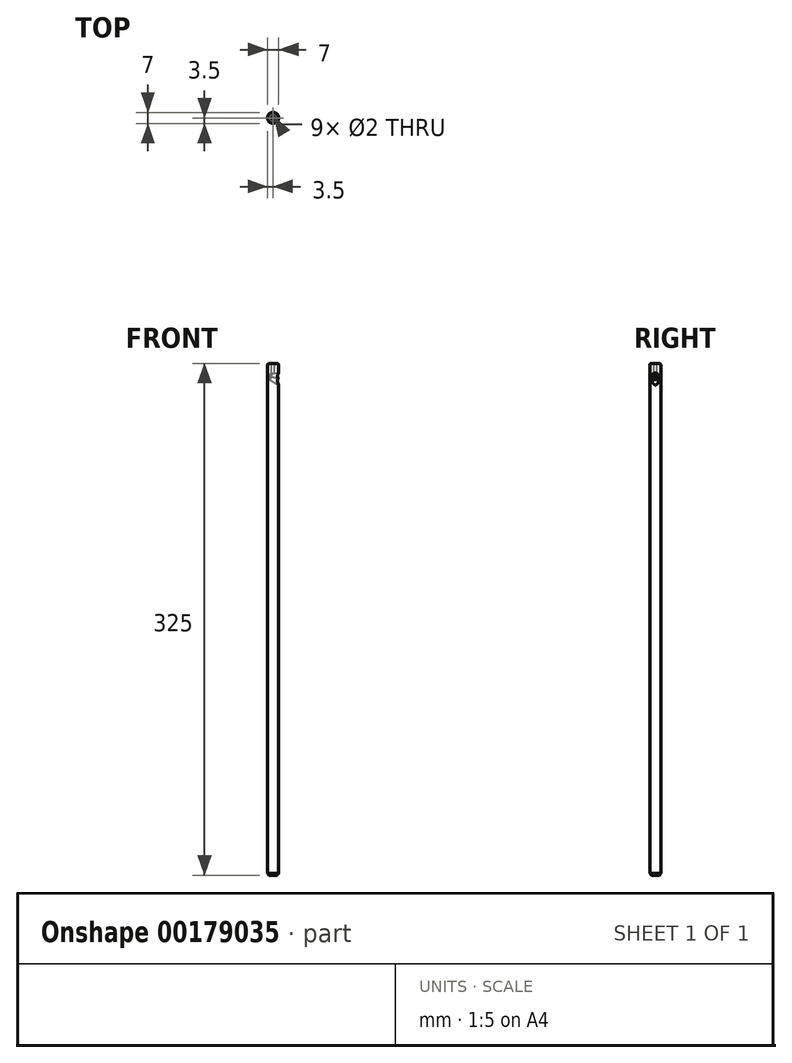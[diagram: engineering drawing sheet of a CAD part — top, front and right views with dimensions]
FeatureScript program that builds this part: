
annotation { "Feature Type Name" : "Feature", "Feature Type Description" : "" }
export const myFeature = defineFeature(function(context is Context, id is Id, definition is map)
    precondition{}
    {
        {
            var Q0;
            Q0=qCreatedBy(makeId("Front.planeOp"),FACE);
            var sketch = newSketch(context, id + "F0", { "sketchPlane" : qUnion([Q0])});
            skLineSegment(sketch, "E0", {"start": v(-3.5, 1) * mm, "end": v(-3.5, 324) * mm});
            skLineSegment(sketch, "E1", {"start": v(-1, 323.5) * mm, "end": v(-1, 318) * mm});
            skLineSegment(sketch, "E2", {"start": v(-1, 318) * mm, "end": v(0, 317.42) * mm});
            skArc(sketch, "E3", {"start": v(-1, 323.5) * mm, "mid": v(-1.44, 324.56) * mm, "end": v(-2.5, 325) * mm});
            skArc(sketch, "E4", {"start": v(-2.5, 325) * mm, "mid": v(-3.2, 324.7) * mm, "end": v(-3.5, 324) * mm});
            skLineSegment(sketch, "E5", {"start": v(-3.5, 1) * mm, "end": v(-2.5, 0) * mm});
            skLineSegment(sketch, "E6", {"start": v(-2.5, 0) * mm, "end": v(0, 0) * mm});
            skPoint(sketch, "E7.orphan", {"position": v(-3.5, 0) * mm});
            skPoint(sketch, "E8.MirrorCS.start.orphan", {"position": v(3.5, 0) * mm});
            skLineSegment(sketch, "E9", {"start": v(0, 317.42) * mm, "end": v(0, 0) * mm});
            skLineSegment(sketch, "E10.MirrorCS", {"start": v(1, 323.5) * mm, "end": v(1, 318) * mm, "construction": true});
            skLineSegment(sketch, "E11", {"start": v(-2.5, 325) * mm, "end": v(1, 325) * mm, "construction": true});
            skSolve(sketch);
        }
        {
            var Q0;
            Q0 = qSketchRegion(id + "F0", true);
            var Q1;
            Q1=sQuery(id+"F0.wireOp",EDGE,"E9");
            revolve(context, id + "F1", {"entities" : qUnion([Q0]), "axis" : qUnion([Q1]), "revolveType" : RevolveType.FULL});
        }
        {
            var Q0;
            Q0=qCreatedBy(makeId("Front.planeOp"),FACE);
            var sketch = newSketch(context, id + "F2", { "sketchPlane" : qUnion([Q0])});
            skLineSegment(sketch, "E12", {"start": v(-2.15, 317) * mm, "end": v(-1, 319) * mm});
            skLineSegment(sketch, "E13", {"start": v(-1, 319) * mm, "end": v(10.58, 319) * mm});
            skLineSegment(sketch, "E14", {"start": v(-2.15, 317) * mm, "end": v(17.02, 317) * mm});
            skLineSegment(sketch, "E15.MirrorCS", {"start": v(-1, 315) * mm, "end": v(10.58, 315) * mm, "construction": true});
            skLineSegment(sketch, "E16.MirrorCS", {"start": v(-2.15, 317) * mm, "end": v(-1, 315) * mm, "construction": true});
            skLineSegment(sketch, "E17", {"start": v(-3.5, 1) * mm, "end": v(-3.5, 324.25) * mm, "construction": true});
            skLineSegment(sketch, "E18", {"start": v(10.58, 319) * mm, "end": v(10.58, 317) * mm});
            skLineSegment(sketch, "E19", {"start": v(1, 323.5) * mm, "end": v(1, 319) * mm, "construction": true});
            skLineSegment(sketch, "E20", {"start": v(-1, 319) * mm, "end": v(-1, 323.5) * mm, "construction": true});
            skLineSegment(sketch, "E21.0", {"start": v(-2.5, 325) * mm, "end": v(2.5, 325) * mm});
            skSolve(sketch);
        }
        {
            var Q0;
            Q0 = qSketchRegion(id + "F2", true);
            var Q1;
            Q1=sQuery(id+"F2.wireOp",EDGE,"E14");
            revolve(context, id + "F3", {"operationType" : NewBodyOperationType.REMOVE, "entities" : qUnion([Q0]), "axis" : qUnion([Q1]), "revolveType" : RevolveType.FULL, "oppositeDirection" : true});
        }
        {
            var Q0;
            Q0=qCreatedBy(makeId("Front.planeOp"),FACE);
            var sketch = newSketch(context, id + "F4", { "sketchPlane" : qUnion([Q0])});
            skLineSegment(sketch, "E22", {"start": v(3.5, 315) * mm, "end": v(-1.25, 315) * mm});
            skLineSegment(sketch, "E23.0", {"start": v(-1, 319) * mm, "end": v(-1, 315) * mm});
            skLineSegment(sketch, "E24", {"start": v(-1.06, 315.1) * mm, "end": v(-2.15, 317) * mm});
            skLineSegment(sketch, "E25", {"start": v(-2.15, 317) * mm, "end": v(-1.06, 318.9) * mm});
            skLineSegment(sketch, "E26", {"start": v(-2.15, 317) * mm, "end": v(-2.15, 314.7) * mm});
            skLineSegment(sketch, "E27", {"start": v(-2.15, 314.7) * mm, "end": v(6.5, 309.7) * mm});
            skLineSegment(sketch, "E28", {"start": v(-2.15, 317) * mm, "end": v(7.5, 311.42) * mm});
            skLineSegment(sketch, "E29", {"start": v(6.5, 309.7) * mm, "end": v(7.5, 311.42) * mm});
            skSolve(sketch);
        }
        {
            var Q0;
            {var subQ7=sQuery(id+"F4.wireOp",EDGE,"E26");Q0=makeQuery(id+"F4.imprint","IMPRINT",FACE,{"disambiguationData":[TD([[makeQuery(id+"F4.imprint","IMPRINT",EDGE,{"derivedFrom":subQ7}),1.0]])]});}
            var Q1;
            {var subQ0=sQuery(id+"F4.wireOp",EDGE,"E23.0");var subQ1=sQuery(id+"F4.wireOp",EDGE,"E22");var subQ2=makeQuery(id+"F4.imprint","INTERSECT",VERTEX,{"derivedFrom":[subQ1,subQ0]});Q1=makeQuery(id+"F4.imprint","IMPRINT",FACE,{"disambiguationData":[TD([[makeQuery(id+"F4.imprint","IMPRINT",EDGE,{"disambiguationData":[TD([[subQ2,1.0]])],"derivedFrom":subQ1}),-1.0]])]});}
            var Q2;
            Q2=sQuery(id+"F4.wireOp",EDGE,"E28");
            revolve(context, id + "F5", {"operationType" : NewBodyOperationType.REMOVE, "entities" : qUnion([Q0, Q1]), "axis" : qUnion([Q2]), "revolveType" : RevolveType.FULL, "oppositeDirection" : true});
        }
    });
